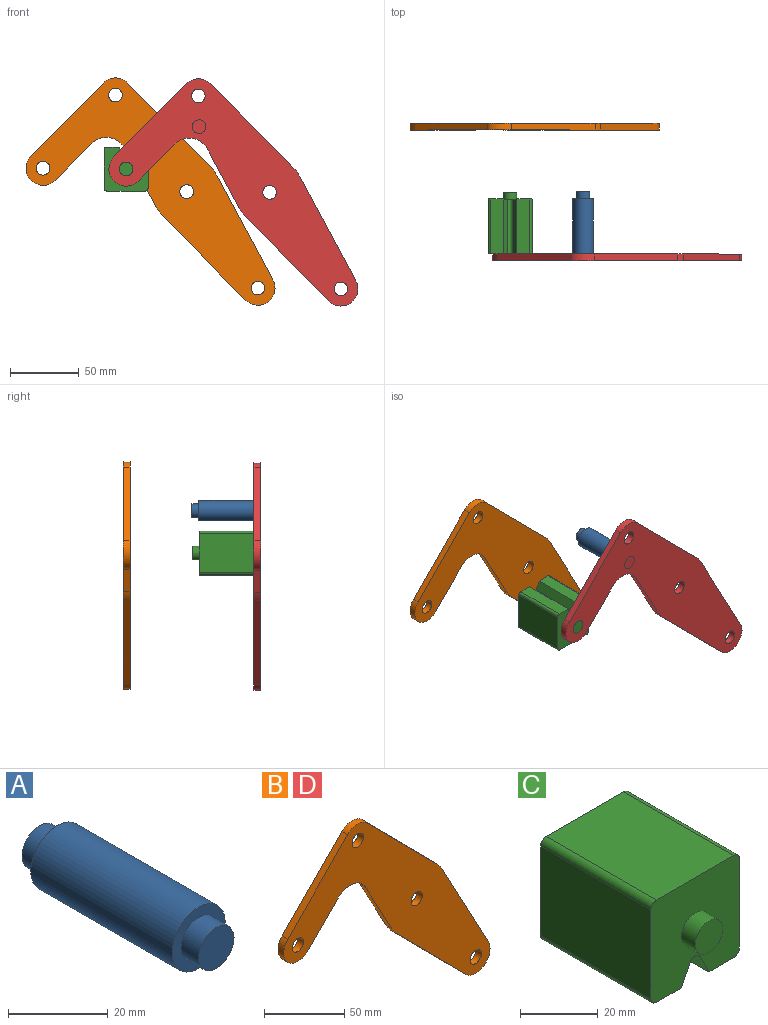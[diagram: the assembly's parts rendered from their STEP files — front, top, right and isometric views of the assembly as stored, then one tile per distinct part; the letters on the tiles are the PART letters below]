
ASSEMBLY  parts=4 mates=1
PART A: 7 faces, bbox 15x50x15 mm
  f0: cylinder r=7.5mm len=40mm, axis (0,-1,0), area 1885mm2, adj f2,f5
  f1: cylinder r=5mm len=10mm, axis (0,1,0), area 157.1mm2, adj f2,f3
  f2: plane 15x15mm, normal (0,-1,0), area 98.2mm2, adj f0,f1
  f3: plane 10x10mm, normal (0,-1,0), area 78.5mm2, adj f1
  f4: cylinder r=5mm len=10mm, axis (0,-1,0), area 157.1mm2, adj f5,f6
  f5: plane 15x15mm, normal (0,1,0), area 98.2mm2, adj f0,f4
  f6: plane 10x10mm, normal (0,1,0), area 78.5mm2, adj f4
PART B: 18 faces, bbox 181.7x5x165.8 mm
  f0: plane 43.49x23.35mm, normal (-0.88,0,-0.47), area 246.8mm2, adj f1,f14,f16,f17
  f1: cylinder r=25mm len=5.75mm, axis (0,1,0), area 35.8mm2, adj f0,f2,f16,f17
  f2: plane 61.6x60.87mm, normal (-0.71,0,-0.7), area 433mm2, adj f1,f3,f16,f17
  f3: cylinder r=12.5mm len=21.39mm, axis (0,1,0), area 178.4mm2, adj f2,f4,f16,f17
  f4: plane 76.3x40.96mm, normal (0.88,0,0.47), area 433mm2, adj f3,f5,f16,f17
  f5: cylinder r=25mm len=5.75mm, axis (0,1,0), area 35.8mm2, adj f4,f6,f16,f17
  f6: plane 61.6x60.87mm, normal (0.71,0,0.7), area 433mm2, adj f5,f7,f16,f17
  f7: cylinder r=12.5mm len=17.78mm, axis (0,1,0), area 98.9mm2, adj f6,f8,f16,f17
  f8: plane 53.35x52.71mm, normal (-0.71,0,0.7), area 375mm2, adj f7,f9,f16,f17
  f9: cylinder r=12.5mm len=21.39mm, axis (0,1,0), area 196.3mm2, adj f8,f10,f16,f17
  f10: plane 26.86x26.54mm, normal (0.71,0,-0.7), area 188.8mm2, adj f9,f14,f16,f17
  f11: cylinder r=5mm len=10mm, axis (0,1,0), area 157.1mm2, adj f16,f17
  f12: cylinder r=5mm len=10mm, axis (0,1,0), area 157.1mm2, adj f16,f17
  f13: cylinder r=5mm len=10mm, axis (0,1,0), area 157.1mm2, adj f16,f17
  f14: cylinder r=15mm len=23.89mm, axis (0,1,0), area 140.2mm2, adj f0,f10,f16,f17
  f15: cylinder r=5mm len=10mm, axis (0,1,0), area 157.1mm2, adj f16,f17
  f16: plane 181.66x165.78mm, normal (0,-1,0), area 8710.1mm2, adj f0,f1,f2,f3,f4,f5,f6,f7
  f17: plane 181.66x165.78mm, normal (0,1,0), area 8710.1mm2, adj f0,f1,f2,f3,f4,f5,f6,f7
PART C: 18 faces, bbox 32.1x50x32.1 mm
  f0: plane 40x28.08mm, normal (1,0,0), area 1123.1mm2, adj f4,f10,f13,f14
  f1: plane 40x9.04mm, normal (0,0,-1), area 361.6mm2, adj f2,f4,f10,f14
  f2: plane 40x6.42mm, normal (-0.89,0,-0.45), area 287.2mm2, adj f1,f4,f10,f15
  f3: plane 40x6.42mm, normal (0.89,0,-0.45), area 287.2mm2, adj f4,f5,f10,f15
  f4: plane 32.08x32.08mm, normal (0,-1,0), area 900.6mm2, adj f0,f1,f2,f3,f5,f6,f7,f9
  f5: plane 40x9.04mm, normal (0,0,-1), area 361.6mm2, adj f3,f4,f10,f16
  f6: plane 40x28.08mm, normal (0,0,1), area 1123.1mm2, adj f4,f10,f13,f17
  f7: plane 40x28.08mm, normal (-1,0,0), area 1123.1mm2, adj f4,f10,f16,f17
  f8: plane 10x10mm, normal (0,-1,0), area 78.5mm2, adj f9
  f9: cylinder r=5mm len=10mm, axis (0,1,0), area 157.1mm2, adj f4,f8
  f10: plane 32.08x32.08mm, normal (0,1,0), area 900.6mm2, adj f0,f1,f2,f3,f5,f6,f7,f12
  f11: plane 10x10mm, normal (0,1,0), area 78.5mm2, adj f12
  f12: cylinder r=5mm len=10mm, axis (0,-1,0), area 157.1mm2, adj f10,f11
  f13: cylinder r=2mm len=40mm, axis (0,1,0), area 125.7mm2, adj f0,f4,f6,f10
  f14: cylinder r=2mm len=40mm, axis (0,-1,0), area 125.7mm2, adj f0,f1,f4,f10
  f15: cylinder r=2mm len=40mm, axis (0,1,0), area 177.1mm2, adj f2,f3,f4,f10
  f16: cylinder r=2mm len=40mm, axis (0,1,0), area 125.7mm2, adj f4,f5,f7,f10
  f17: cylinder r=2mm len=40mm, axis (0,-1,0), area 125.7mm2, adj f4,f6,f7,f10
PART D: same geometry as B
PLACE A t=(30.62,-22.79,12.62)mm
PLACE B t=(-30.42,72.31,35.64)mm
PLACE C rot(axis=(1,0,0),180deg) t=(30.09,16.99,69.14)mm
PLACE D t=(30.09,-23.01,35.06)mm fixed
MATE fastened C.f9 <-> D.f9  axis (0,-1,0) through (-74.6,-23.01,52.1)mm
